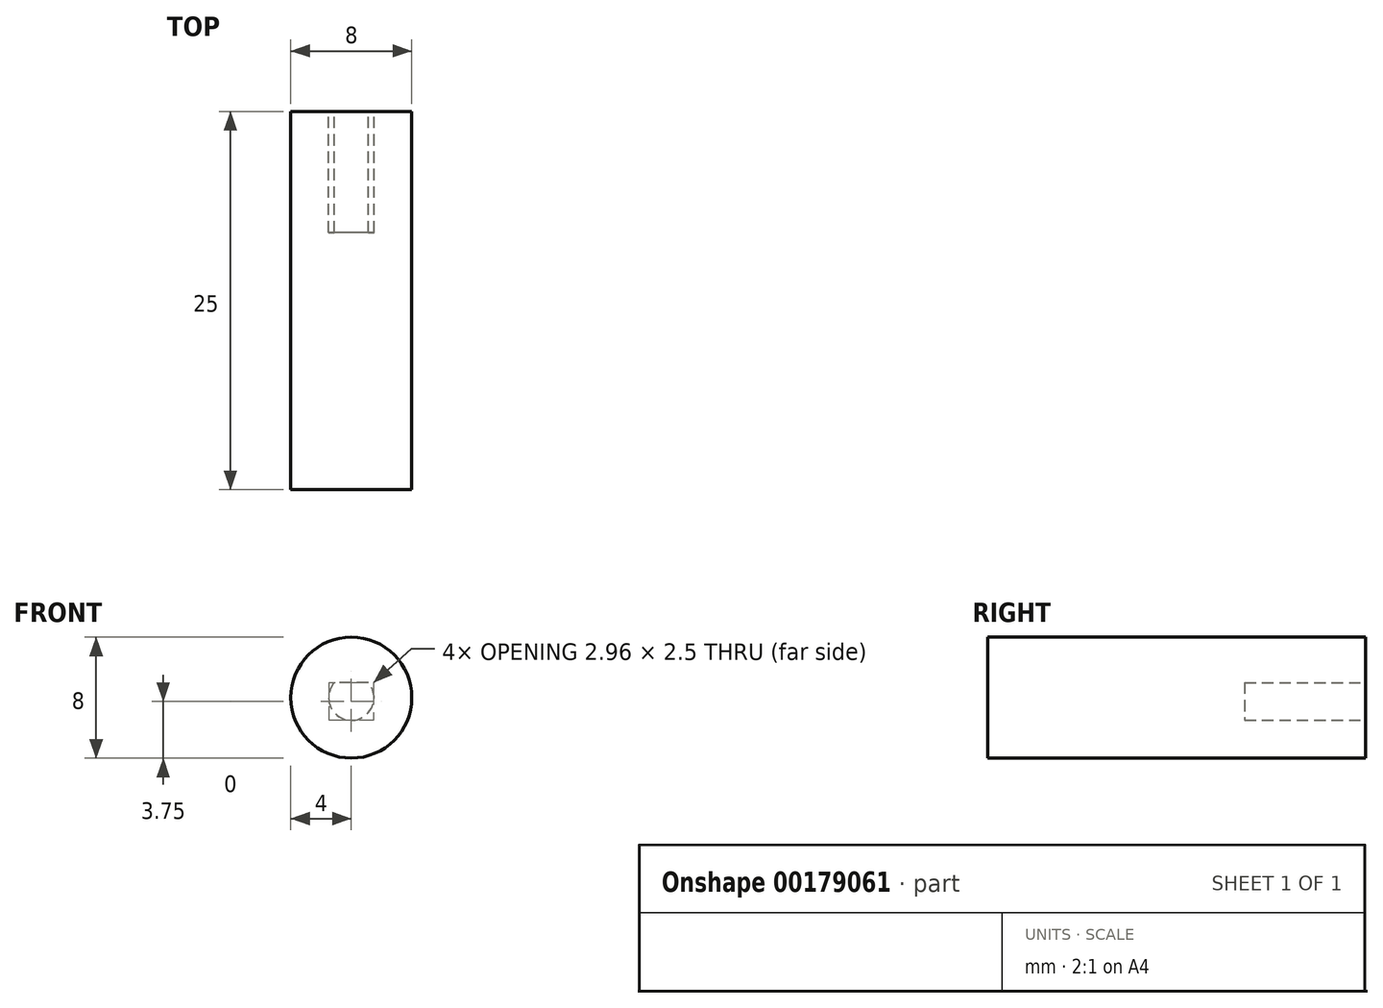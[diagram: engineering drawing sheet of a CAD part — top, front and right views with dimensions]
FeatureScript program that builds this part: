
annotation { "Feature Type Name" : "Feature", "Feature Type Description" : "" }
export const myFeature = defineFeature(function(context is Context, id is Id, definition is map)
    precondition{}
    {
        {
            var Q0;
            Q0=qCreatedBy(makeId("Front.planeOp"),FACE);
            var sketch = newSketch(context, id + "F0", { "sketchPlane" : qUnion([Q0])});
            skCircle(sketch, "E0", {"center": v(0, 0) * mm, "radius": 4 * mm});
            skSolve(sketch);
        }
        {
            var Q0;
            Q0 = qSketchRegion(id + "F0", true);
            extrude(context, id + "F1", {"entities" : qUnion([Q0]), "depth" : 25 * mm});
        }
        {
            var Q0;
            Q0=makeQuery(id+"F1.opExtrude","CAP_FACE",FACE,{"disambiguationData":[OSD([sQuery(id+"F0.wireOp",EDGE,"E0")])],"isStart":true});
            var sketch = newSketch(context, id + "F2", { "sketchPlane" : qUnion([Q0])});
            skLineSegment(sketch, "E1", {"start": v(-1.12, 1) * mm, "end": v(1.12, 1) * mm});
            skArc(sketch, "E2", {"start": v(-1.12, 1) * mm, "mid": v(0, -1.5) * mm, "end": v(1.12, 1) * mm});
            skArc(sketch, "E3", {"start": v(1.12, 1) * mm, "mid": v(0, 1.5) * mm, "end": v(-1.12, 1) * mm, "construction": true});
            skSolve(sketch);
        }
        {
            var Q0;
            Q0 = qSketchRegion(id + "F2", true);
            extrude(context, id + "F3", {"entities" : qUnion([Q0]), "operationType" : NewBodyOperationType.REMOVE, "oppositeDirection" : true, "depth" : 8 * mm});
        }
    });
